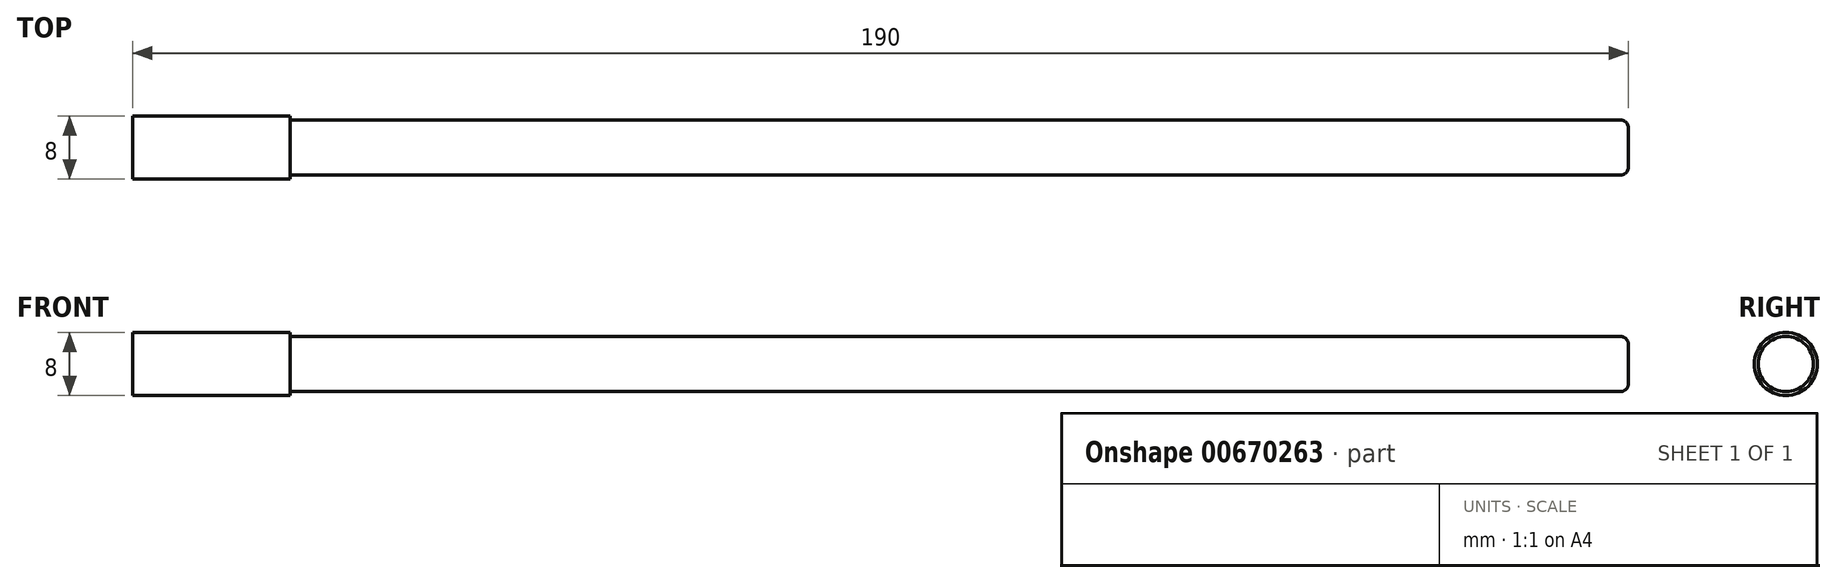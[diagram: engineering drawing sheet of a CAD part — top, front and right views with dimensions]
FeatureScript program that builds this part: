
annotation { "Feature Type Name" : "Feature", "Feature Type Description" : "" }
export const myFeature = defineFeature(function(context is Context, id is Id, definition is map)
    precondition{}
    {
        {
            var Q0;
            Q0=qCreatedBy(makeId("Right.planeOp"),FACE);
            var sketch = newSketch(context, id + "F0", { "sketchPlane" : qUnion([Q0])});
            skCircle(sketch, "E0", {"center": v(0, 0) * mm, "radius": 4 * mm});
            skSolve(sketch);
        }
        {
            var Q0;
            Q0=makeQuery(id+"F0.imprint","IMPRINT",FACE,{"disambiguationData":[TD([[makeQuery(id+"F0.imprint","IMPRINT",EDGE,{"derivedFrom":sQuery(id+"F0.wireOp",EDGE,"E0")}),1.0]])]});
            extrude(context, id + "F1", {"entities" : qUnion([Q0]), "depth" : 20 * mm, "offsetDistance" : 25 * mm});
        }
        {
            var Q0;
            Q0=makeQuery(id+"F1.opExtrude","CAP_FACE",FACE,{"disambiguationData":[OSD([sQuery(id+"F0.wireOp",EDGE,"E0")])],"isStart":false});
            var sketch = newSketch(context, id + "F2", { "sketchPlane" : qUnion([Q0])});
            skCircle(sketch, "E1", {"center": v(0, 0) * mm, "radius": 3.5 * mm});
            skSolve(sketch);
        }
        {
            var Q0;
            Q0=makeQuery(id+"F2.imprint","IMPRINT",FACE,{"disambiguationData":[TD([[makeQuery(id+"F2.imprint","IMPRINT",EDGE,{"derivedFrom":sQuery(id+"F2.wireOp",EDGE,"E1")}),1.0]])]});
            extrude(context, id + "F3", {"entities" : qUnion([Q0]), "operationType" : NewBodyOperationType.ADD, "depth" : 170 * mm, "offsetDistance" : 25 * mm});
        }
        {
            var Q0;
            Q0=makeQuery(id+"F3.opExtrude","CAP_FACE",FACE,{"disambiguationData":[OSD([sQuery(id+"F2.wireOp",EDGE,"E1")])],"isStart":false});
            fillet(context, id + "F4", {"entities" : qUnion([Q0]), "radius" : 1 * mm, "tangentPropagation" : true, "allowEdgeOverflow" : false});
        }
    });
